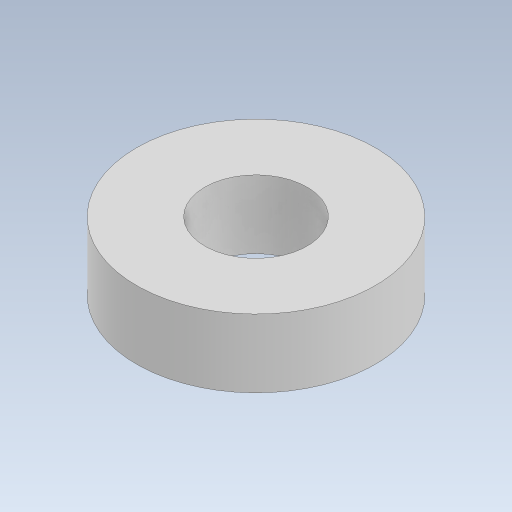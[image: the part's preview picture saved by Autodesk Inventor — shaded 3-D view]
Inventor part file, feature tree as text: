
AUTODESK INVENTOR PART (.ipt)
format: ipt  version: 2023.5 (Build 275446000, 446)  size: 249,856 bytes
history: native  units: mm
features: extrude x1, sketch x1
ambient origin geometry x8: Origin, YZ Plane, XZ Plane, XY Plane, X Axis, Y Axis, Z Axis, Center Point
bodies: Solid1 (feature_tree)
feature tree (2):
  extrude  "Extrusion1"  Depth=2.0mm
  sketch  "Sketch1"  dims[d0=3.0mm d1=7.0mm d2=2.0mm d3=0.0mm]
